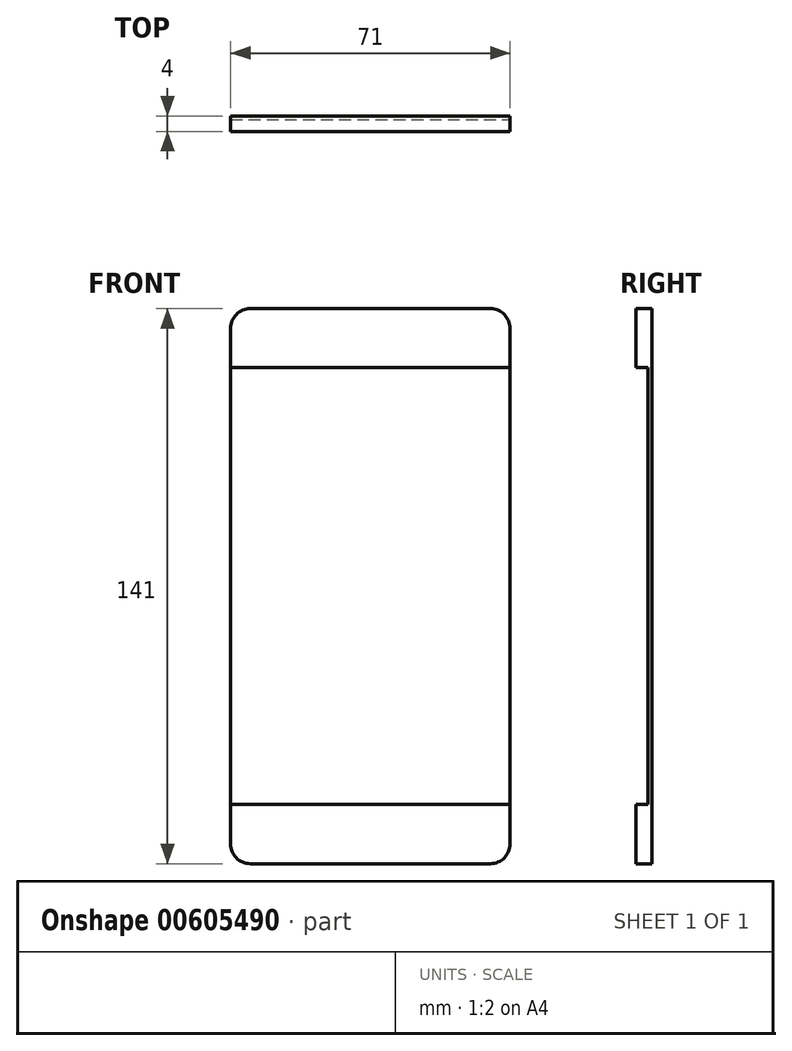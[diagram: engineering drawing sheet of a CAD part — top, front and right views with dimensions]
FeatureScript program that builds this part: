
annotation { "Feature Type Name" : "Feature", "Feature Type Description" : "" }
export const myFeature = defineFeature(function(context is Context, id is Id, definition is map)
    precondition{}
    {
        {
            var Q0;
            Q0=qCreatedBy(makeId("Front.planeOp"),FACE);
            var sketch = newSketch(context, id + "F0", { "sketchPlane" : qUnion([Q0])});
            skLineSegment(sketch, "E0.bottom", {"start": v(-35.5, -70.5) * mm, "end": v(35.5, -70.5) * mm});
            skLineSegment(sketch, "E0.top", {"start": v(-35.5, 70.5) * mm, "end": v(35.5, 70.5) * mm});
            skLineSegment(sketch, "E0.left", {"start": v(-35.5, -70.5) * mm, "end": v(-35.5, 70.5) * mm});
            skLineSegment(sketch, "E0.right", {"start": v(35.5, -70.5) * mm, "end": v(35.5, 70.5) * mm});
            skPoint(sketch, "E0.middle", {"position": v(0, 0) * mm});
            skLineSegment(sketch, "E1.top", {"start": v(-35.5, 55.5) * mm, "end": v(35.5, 55.5) * mm});
            skLineSegment(sketch, "E1.left", {"start": v(-35.5, 70.5) * mm, "end": v(-35.5, 55.5) * mm});
            skLineSegment(sketch, "E1.right", {"start": v(35.5, 70.5) * mm, "end": v(35.5, 55.5) * mm});
            skLineSegment(sketch, "E2.top", {"start": v(-35.5, -55.5) * mm, "end": v(35.5, -55.5) * mm});
            skLineSegment(sketch, "E2.left", {"start": v(-35.5, -70.5) * mm, "end": v(-35.5, -55.5) * mm});
            skLineSegment(sketch, "E2.right", {"start": v(35.5, -70.5) * mm, "end": v(35.5, -55.5) * mm});
            skSolve(sketch);
        }
        {
            var Q0;
            Q0=makeQuery(id+"F0.imprint","IMPRINT",FACE,{"disambiguationData":[TD([[makeQuery(id+"F0.imprint","IMPRINT",EDGE,{"derivedFrom":sQuery(id+"F0.wireOp",EDGE,"E0.top")}),-1.0]])]});
            var Q1;
            Q1=makeQuery(id+"F0.imprint","IMPRINT",FACE,{"disambiguationData":[TD([[makeQuery(id+"F0.imprint","IMPRINT",EDGE,{"derivedFrom":sQuery(id+"F0.wireOp",EDGE,"E0.bottom")}),1.0]])]});
            extrude(context, id + "F1", {"entities" : qUnion([Q0, Q1]), "depth" : 4 * mm, "offsetDistance" : 25 * mm});
        }
        {
            var Q0;
            Q0=makeQuery(id+"F0.imprint","IMPRINT",FACE,{"disambiguationData":[TD([[makeQuery(id+"F0.imprint","IMPRINT",EDGE,{"derivedFrom":sQuery(id+"F0.wireOp",EDGE,"E0.left")}),-1.0]])]});
            extrude(context, id + "F2", {"entities" : qUnion([Q0]), "operationType" : NewBodyOperationType.ADD, "depth" : 1 * mm, "offsetDistance" : 25 * mm});
        }
        {
            var Q0;
            Q0=makeQuery(id+"F1.opExtrude","SWEPT_EDGE",EDGE,{"disambiguationData":[OSD([sQuery(id+"F0.wireOp",EDGE,"E0.top"),sQuery(id+"F0.wireOp",EDGE,"E1.left")])]});
            var Q1;
            Q1=makeQuery(id+"F1.opExtrude","SWEPT_EDGE",EDGE,{"disambiguationData":[OSD([sQuery(id+"F0.wireOp",EDGE,"E0.top"),sQuery(id+"F0.wireOp",EDGE,"E1.right")])]});
            var Q2;
            Q2=makeQuery(id+"F1.opExtrude","SWEPT_EDGE",EDGE,{"disambiguationData":[OSD([sQuery(id+"F0.wireOp",EDGE,"E0.bottom"),sQuery(id+"F0.wireOp",EDGE,"E2.right")])]});
            var Q3;
            Q3=makeQuery(id+"F1.opExtrude","SWEPT_EDGE",EDGE,{"disambiguationData":[OSD([sQuery(id+"F0.wireOp",EDGE,"E0.bottom"),sQuery(id+"F0.wireOp",EDGE,"E2.left")])]});
            fillet(context, id + "F3", {"entities" : qUnion([Q0, Q1, Q2, Q3]), "radius" : 5 * mm, "tangentPropagation" : true, "allowEdgeOverflow" : false});
        }
    });
